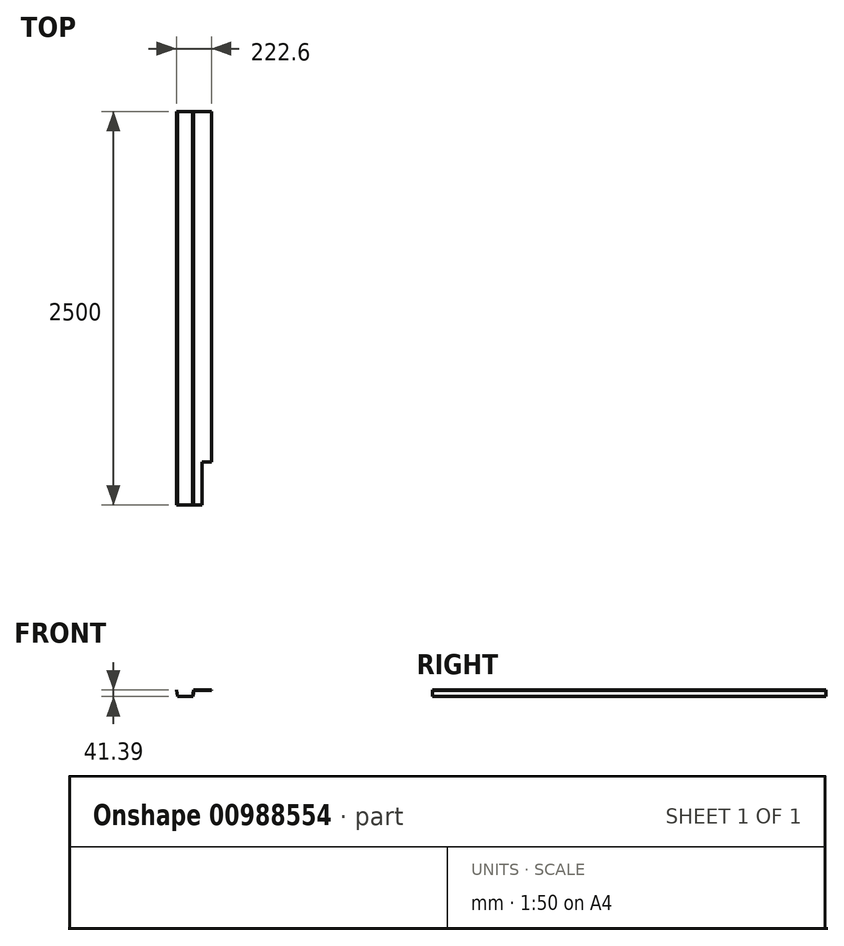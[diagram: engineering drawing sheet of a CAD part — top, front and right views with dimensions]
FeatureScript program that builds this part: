
annotation { "Feature Type Name" : "Feature", "Feature Type Description" : "" }
export const myFeature = defineFeature(function(context is Context, id is Id, definition is map)
    precondition{}
    {
        {
            var Q0;
            Q0=qCreatedBy(makeId("Front.planeOp"),FACE);
            var sketch = newSketch(context, id + "F0", { "sketchPlane" : qUnion([Q0])});
            skLineSegment(sketch, "E0", {"start": v(-54.7, 24.35) * mm, "end": v(-47.76, -15.04) * mm});
            skLineSegment(sketch, "E1", {"start": v(-47.76, -15.04) * mm, "end": v(47.24, -15.04) * mm});
            skLineSegment(sketch, "E2", {"start": v(47.24, -15.04) * mm, "end": v(54.18, 24.35) * mm});
            skLineSegment(sketch, "E3", {"start": v(54.18, 24.35) * mm, "end": v(115.86, 24.35) * mm});
            skLineSegment(sketch, "E4.0", {"start": v(55.86, 22.35) * mm, "end": v(115.86, 22.35) * mm});
            skLineSegment(sketch, "E4.1", {"start": v(48.92, -17.04) * mm, "end": v(55.86, 22.35) * mm});
            skLineSegment(sketch, "E4.2", {"start": v(-49.44, -17.04) * mm, "end": v(48.92, -17.04) * mm});
            skLineSegment(sketch, "E4.3", {"start": v(-56.74, 24.35) * mm, "end": v(-49.44, -17.04) * mm});
            skLineSegment(sketch, "E5", {"start": v(115.86, 24.35) * mm, "end": v(115.86, 22.35) * mm});
            skLineSegment(sketch, "E6", {"start": v(-54.7, 24.35) * mm, "end": v(-56.74, 24.35) * mm});
            skSolve(sketch);
        }
        {
            var Q0;
            Q0=makeQuery(id+"F0.imprint","IMPRINT",FACE,{"disambiguationData":[TD([[makeQuery(id+"F0.imprint","IMPRINT",EDGE,{"derivedFrom":sQuery(id+"F0.wireOp",EDGE,"E0")}),-1.0]])]});
            extrude(context, id + "F1", {"entities" : qUnion([Q0]), "depth" : 2500 * mm, "offsetDistance" : 25 * mm});
        }
        {
            var Q0;
            Q0=makeQuery(id+"F1.opExtrude","SWEPT_FACE",FACE,{"disambiguationData":[OSD([sQuery(id+"F0.wireOp",EDGE,"E5")])]});
            extrude(context, id + "F2", {"entities" : qUnion([Q0]), "operationType" : NewBodyOperationType.ADD, "depth" : 50 * mm, "offsetDistance" : 25 * mm});
        }
        {
            var Q0;
            {var subQ0=sQuery(id+"F0.wireOp",EDGE,"E5");Q0=makeQuery(id+"F2.boolean.opBoolean","MERGE",FACE,{"derivedFrom":[makeQuery(id+"F1.opExtrude","CAP_FACE",FACE,{"disambiguationData":[OSD([sQuery(id+"F0.wireOp",EDGE,"E0"),sQuery(id+"F0.wireOp",EDGE,"E1"),sQuery(id+"F0.wireOp",EDGE,"E2"),sQuery(id+"F0.wireOp",EDGE,"E3"),sQuery(id+"F0.wireOp",EDGE,"E4.0"),sQuery(id+"F0.wireOp",EDGE,"E4.1"),sQuery(id+"F0.wireOp",EDGE,"E4.2"),sQuery(id+"F0.wireOp",EDGE,"E4.3"),subQ0,sQuery(id+"F0.wireOp",EDGE,"E6")])],"isStart":false}),makeQuery(id+"F2.opExtrude","SWEPT_FACE",FACE,{"disambiguationData":[OSD([subQ0]),TDD([makeQuery(id+"F1.opExtrude","CAP_EDGE",EDGE,{"disambiguationData":[OSD([subQ0])],"isStart":false})])]})]});}
            var sketch = newSketch(context, id + "F3", { "sketchPlane" : qUnion([Q0])});
            skLineSegment(sketch, "E7.bottom", {"start": v(165.86, 22.35) * mm, "end": v(105.67, 22.35) * mm});
            skLineSegment(sketch, "E7.top", {"start": v(165.86, 24.35) * mm, "end": v(105.67, 24.35) * mm});
            skLineSegment(sketch, "E7.left", {"start": v(165.86, 22.35) * mm, "end": v(165.86, 24.35) * mm});
            skLineSegment(sketch, "E7.right", {"start": v(105.67, 22.35) * mm, "end": v(105.67, 24.35) * mm});
            skSolve(sketch);
        }
        {
            var Q0;
            Q0=makeQuery(id+"F3.imprint","IMPRINT",FACE,{"disambiguationData":[TD([[makeQuery(id+"F3.imprint","IMPRINT",EDGE,{"derivedFrom":sQuery(id+"F3.wireOp",EDGE,"E7.bottom")}),1.0]])]});
            extrude(context, id + "F4", {"entities" : qUnion([Q0]), "operationType" : NewBodyOperationType.REMOVE, "oppositeDirection" : true, "depth" : 275 * mm, "offsetDistance" : 25 * mm});
        }
    });
